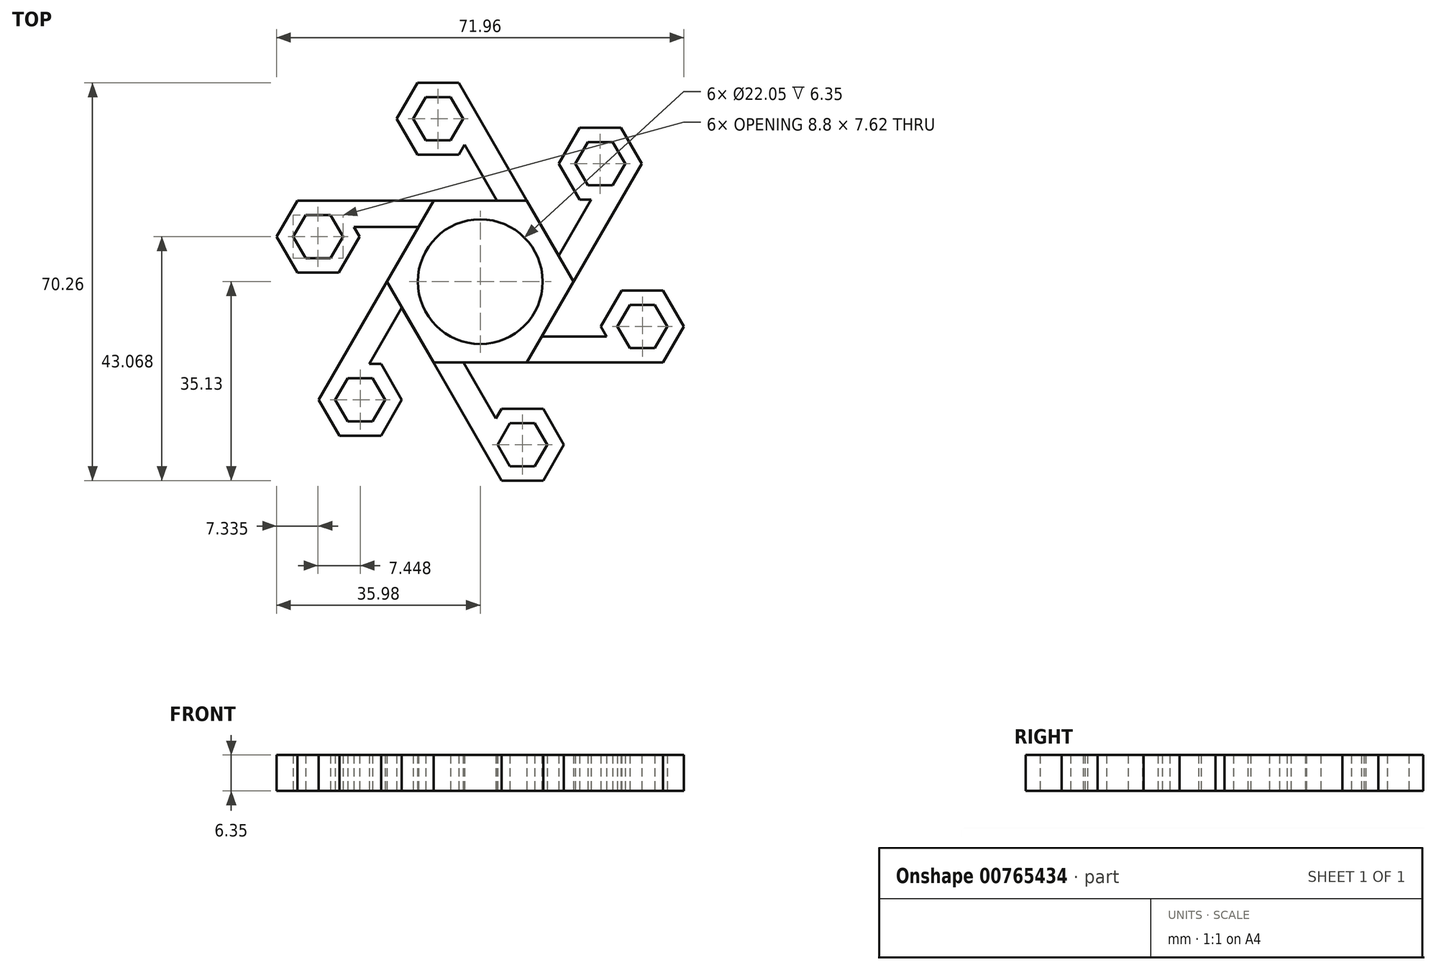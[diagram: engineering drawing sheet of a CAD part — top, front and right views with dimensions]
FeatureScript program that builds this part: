
annotation { "Feature Type Name" : "Feature", "Feature Type Description" : "" }
export const myFeature = defineFeature(function(context is Context, id is Id, definition is map)
    precondition{}
    {
        {
            var Q0;
            Q0=qCreatedBy(makeId("Top.planeOp"),FACE);
            var sketch = newSketch(context, id + "F0", { "sketchPlane" : qUnion([Q0])});
            skCircle(sketch, "E0.cCircle", {"center": v(0, 0) * mm, "radius": 14.29 * mm, "construction": true});
            skLineSegment(sketch, "E0.0", {"start": v(8.25, -14.29) * mm, "end": v(-8.25, -14.29) * mm});
            skLineSegment(sketch, "E0.1", {"start": v(-8.25, -14.29) * mm, "end": v(-16.5, 0) * mm});
            skLineSegment(sketch, "E0.2", {"start": v(-16.5, 0) * mm, "end": v(-8.25, 14.29) * mm});
            skLineSegment(sketch, "E0.3", {"start": v(-8.25, 14.29) * mm, "end": v(8.25, 14.29) * mm});
            skLineSegment(sketch, "E0.4", {"start": v(8.25, 14.29) * mm, "end": v(16.5, 0) * mm});
            skLineSegment(sketch, "E0.5", {"start": v(16.5, 0) * mm, "end": v(8.25, -14.29) * mm});
            skPoint(sketch, "E0.0.midPoint", {"position": v(0, -14.29) * mm});
            skCircle(sketch, "E1", {"center": v(0, 0) * mm, "radius": 11.02 * mm});
            skLineSegment(sketch, "E2", {"start": v(-8.25, -14.29) * mm, "end": v(3.78, -35.13) * mm});
            skLineSegment(sketch, "E3", {"start": v(-2.95, -14.29) * mm, "end": v(2.77, -24.19) * mm});
            skCircle(sketch, "E4.cCircle", {"center": v(7.45, -28.78) * mm, "radius": 6.35 * mm, "construction": true});
            skLineSegment(sketch, "E4.0", {"start": v(3.78, -35.13) * mm, "end": v(0.12, -28.78) * mm});
            skLineSegment(sketch, "E4.1", {"start": v(0.12, -28.78) * mm, "end": v(3.78, -22.43) * mm});
            skLineSegment(sketch, "E4.2", {"start": v(3.78, -22.43) * mm, "end": v(11.11, -22.43) * mm});
            skLineSegment(sketch, "E4.3", {"start": v(11.11, -22.43) * mm, "end": v(14.78, -28.78) * mm});
            skLineSegment(sketch, "E4.4", {"start": v(14.78, -28.78) * mm, "end": v(11.11, -35.13) * mm});
            skLineSegment(sketch, "E4.5", {"start": v(11.11, -35.13) * mm, "end": v(3.78, -35.13) * mm});
            skPoint(sketch, "E4.0.midPoint", {"position": v(1.95, -31.95) * mm});
            skCircle(sketch, "E5.cCircle", {"center": v(7.45, -28.78) * mm, "radius": 3.81 * mm, "construction": true});
            skLineSegment(sketch, "E5.0", {"start": v(9.65, -32.59) * mm, "end": v(5.25, -32.59) * mm});
            skLineSegment(sketch, "E5.1", {"start": v(5.25, -32.59) * mm, "end": v(3.05, -28.78) * mm});
            skLineSegment(sketch, "E5.2", {"start": v(3.05, -28.78) * mm, "end": v(5.25, -24.97) * mm});
            skLineSegment(sketch, "E5.3", {"start": v(5.25, -24.97) * mm, "end": v(9.65, -24.97) * mm});
            skLineSegment(sketch, "E5.4", {"start": v(9.65, -24.97) * mm, "end": v(11.85, -28.78) * mm});
            skLineSegment(sketch, "E5.5", {"start": v(11.85, -28.78) * mm, "end": v(9.65, -32.59) * mm});
            skPoint(sketch, "E5.0.midPoint", {"position": v(7.45, -32.59) * mm});
            skSolve(sketch);
        }
        {
            var Q0;
            {var subQ0=sQuery(id+"F0.wireOp",EDGE,"E0.1");Q0=makeQuery(id+"F0.imprint","IMPRINT",FACE,{"disambiguationData":[TD([[makeQuery(id+"F0.imprint","IMPRINT",EDGE,{"derivedFrom":subQ0}),-1.0]])]});}
            var Q1;
            {var subQ3=sQuery(id+"F0.wireOp",EDGE,"E3");Q1=makeQuery(id+"F0.imprint","IMPRINT",FACE,{"disambiguationData":[TD([[makeQuery(id+"F0.imprint","IMPRINT",EDGE,{"derivedFrom":subQ3}),-1.0]])]});}
            var Q2;
            {var subQ5=sQuery(id+"F0.wireOp",EDGE,"E4.2");Q2=makeQuery(id+"F0.imprint","IMPRINT",FACE,{"disambiguationData":[TD([[makeQuery(id+"F0.imprint","IMPRINT",EDGE,{"derivedFrom":subQ5}),-1.0]])]});}
            extrude(context, id + "F1", {"entities" : qUnion([Q0, Q1, Q2]), "depth" : 6.35 * mm, "offsetDistance" : 25.4 * mm});
        }
        {
            var Q0;
            Q0=makeQuery(id+"F1.opExtrude","SWEPT_BODY",BODY,{"disambiguationData":[OSD([sQuery(id+"F0.wireOp",EDGE,"E0.0"),sQuery(id+"F0.wireOp",EDGE,"E0.1"),sQuery(id+"F0.wireOp",EDGE,"E0.2"),sQuery(id+"F0.wireOp",EDGE,"E0.3"),sQuery(id+"F0.wireOp",EDGE,"E0.4"),sQuery(id+"F0.wireOp",EDGE,"E0.5"),sQuery(id+"F0.wireOp",EDGE,"E1"),sQuery(id+"F0.wireOp",EDGE,"E2"),sQuery(id+"F0.wireOp",EDGE,"E3"),sQuery(id+"F0.wireOp",EDGE,"E4.1"),sQuery(id+"F0.wireOp",EDGE,"E4.2"),sQuery(id+"F0.wireOp",EDGE,"E4.3"),sQuery(id+"F0.wireOp",EDGE,"E4.4"),sQuery(id+"F0.wireOp",EDGE,"E4.5"),sQuery(id+"F0.wireOp",EDGE,"E5.0"),sQuery(id+"F0.wireOp",EDGE,"E5.1"),sQuery(id+"F0.wireOp",EDGE,"E5.2"),sQuery(id+"F0.wireOp",EDGE,"E5.3"),sQuery(id+"F0.wireOp",EDGE,"E5.4"),sQuery(id+"F0.wireOp",EDGE,"E5.5")])]});
            var Q1;
            Q1=makeQuery(id+"F1.opExtrude","CAP_EDGE",EDGE,{"disambiguationData":[OSD([sQuery(id+"F0.wireOp",EDGE,"E1")])],"isStart":false});
            circularPattern(context, id + "F2", {"entities" : qUnion([Q0]), "axis" : qUnion([Q1]), "angle" : 360 * degree, "instanceCount" : 6, "equalSpace" : true});
        }
    });
